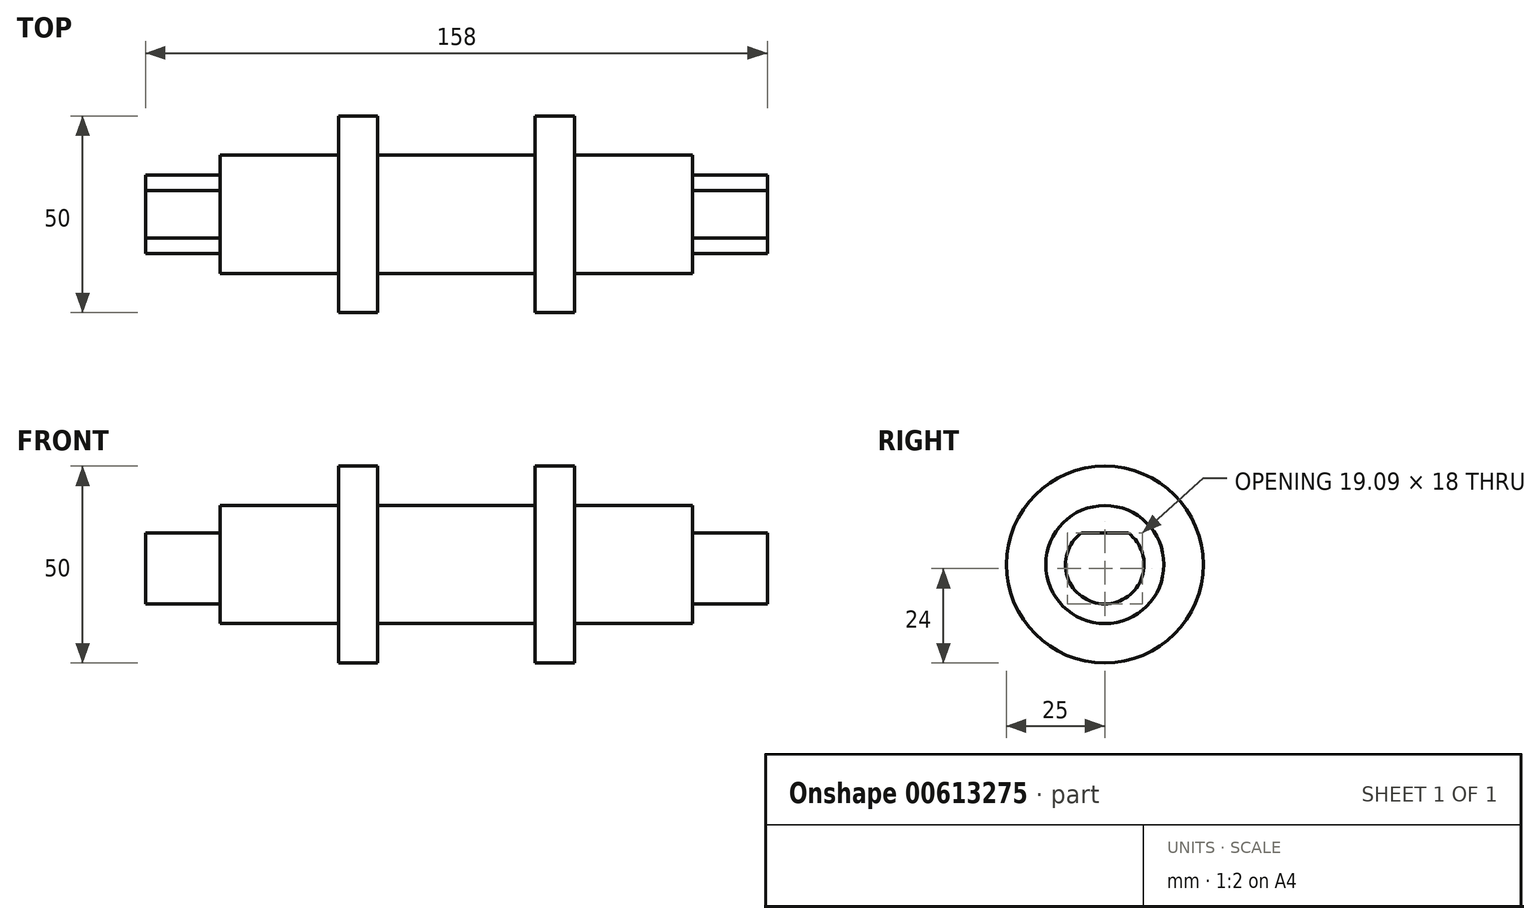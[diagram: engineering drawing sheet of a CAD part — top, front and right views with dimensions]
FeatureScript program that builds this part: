
annotation { "Feature Type Name" : "Feature", "Feature Type Description" : "" }
export const myFeature = defineFeature(function(context is Context, id is Id, definition is map)
    precondition{}
    {
        {
            var Q0;
            Q0=qCreatedBy(makeId("Right.planeOp"),FACE);
            var sketch = newSketch(context, id + "F0", { "sketchPlane" : qUnion([Q0])});
            skCircle(sketch, "E0", {"center": v(0, 0) * mm, "radius": 10 * mm});
            skSolve(sketch);
        }
        {
            var Q0;
            Q0 = qSketchRegion(id + "F0", true);
            extrude(context, id + "F1", {"entities" : qUnion([Q0]), "depth" : 19 * mm, "offsetDistance" : 25 * mm});
        }
        {
            var Q0;
            Q0=makeQuery(id+"F1.opExtrude","CAP_FACE",FACE,{"disambiguationData":[OSD([sQuery(id+"F0.wireOp",EDGE,"E0")])],"isStart":false});
            var sketch = newSketch(context, id + "F2", { "sketchPlane" : qUnion([Q0])});
            skCircle(sketch, "E1", {"center": v(0, 0) * mm, "radius": 15 * mm});
            skSolve(sketch);
        }
        {
            var Q0;
            Q0 = qSketchRegion(id + "F2", true);
            extrude(context, id + "F3", {"entities" : qUnion([Q0]), "operationType" : NewBodyOperationType.ADD, "depth" : 30 * mm, "offsetDistance" : 25 * mm});
        }
        {
            var Q0;
            Q0=makeQuery(id+"F3.opExtrude","CAP_FACE",FACE,{"disambiguationData":[OSD([sQuery(id+"F2.wireOp",EDGE,"E1")])],"isStart":false});
            var sketch = newSketch(context, id + "F4", { "sketchPlane" : qUnion([Q0])});
            skCircle(sketch, "E2", {"center": v(0, 0) * mm, "radius": 25 * mm});
            skSolve(sketch);
        }
        {
            var Q0;
            Q0 = qSketchRegion(id + "F4", true);
            extrude(context, id + "F5", {"entities" : qUnion([Q0]), "operationType" : NewBodyOperationType.ADD, "depth" : 10 * mm, "offsetDistance" : 25 * mm});
        }
        {
            var Q0;
            Q0=makeQuery(id+"F5.opExtrude","CAP_FACE",FACE,{"disambiguationData":[OSD([sQuery(id+"F4.wireOp",EDGE,"E2")])],"isStart":false});
            var sketch = newSketch(context, id + "F6", { "sketchPlane" : qUnion([Q0])});
            skCircle(sketch, "E3", {"center": v(0, 0) * mm, "radius": 15 * mm});
            skSolve(sketch);
        }
        {
            var Q0;
            Q0 = qSketchRegion(id + "F6", true);
            extrude(context, id + "F7", {"entities" : qUnion([Q0]), "operationType" : NewBodyOperationType.ADD, "depth" : 20 * mm, "offsetDistance" : 25 * mm});
        }
        {
            var Q0;
            Q0=makeQuery(id+"F1.opExtrude","CAP_FACE",FACE,{"disambiguationData":[OSD([sQuery(id+"F0.wireOp",EDGE,"E0")])],"isStart":true});
            var sketch = newSketch(context, id + "F8", { "sketchPlane" : qUnion([Q0])});
            skLineSegment(sketch, "E4", {"start": v(-6, 8) * mm, "end": v(6, 8) * mm});
            skSolve(sketch);
        }
        {
            var Q0;
            {var subQ0=sQuery(id+"F8.wireOp",EDGE,"E4");Q0=makeQuery(id+"F8.imprint","IMPRINT",FACE,{"disambiguationData":[TD([[makeQuery(id+"F8.imprint","IMPRINT",EDGE,{"derivedFrom":subQ0}),1.0]])]});}
            var Q1;
            Q1=makeQuery(id+"F3.opExtrude","CAP_FACE",FACE,{"disambiguationData":[OSD([sQuery(id+"F2.wireOp",EDGE,"E1")])],"isStart":true});
            extrude(context, id + "F9", {"entities" : qUnion([Q0]), "operationType" : NewBodyOperationType.REMOVE, "endBound" : BoundingType.UP_TO_SURFACE, "oppositeDirection" : true, "depth" : 25 * mm, "endBoundEntityFace" : qUnion([Q1]), "offsetDistance" : 25 * mm});
        }
        {
            var Q0;
            Q0=makeQuery(id+"F1.opExtrude","SWEPT_BODY",BODY,{"disambiguationData":[OSD([sQuery(id+"F0.wireOp",EDGE,"E0")])]});
            var Q1;
            Q1=makeQuery(id+"F7.opExtrude","CAP_FACE",FACE,{"disambiguationData":[OSD([sQuery(id+"F6.wireOp",EDGE,"E3")])],"isStart":false});
            mirror(context, id + "F10", {"operationType" : NewBodyOperationType.ADD, "entities" : qUnion([Q0]), "mirrorPlane" : qUnion([Q1])});
        }
    });
